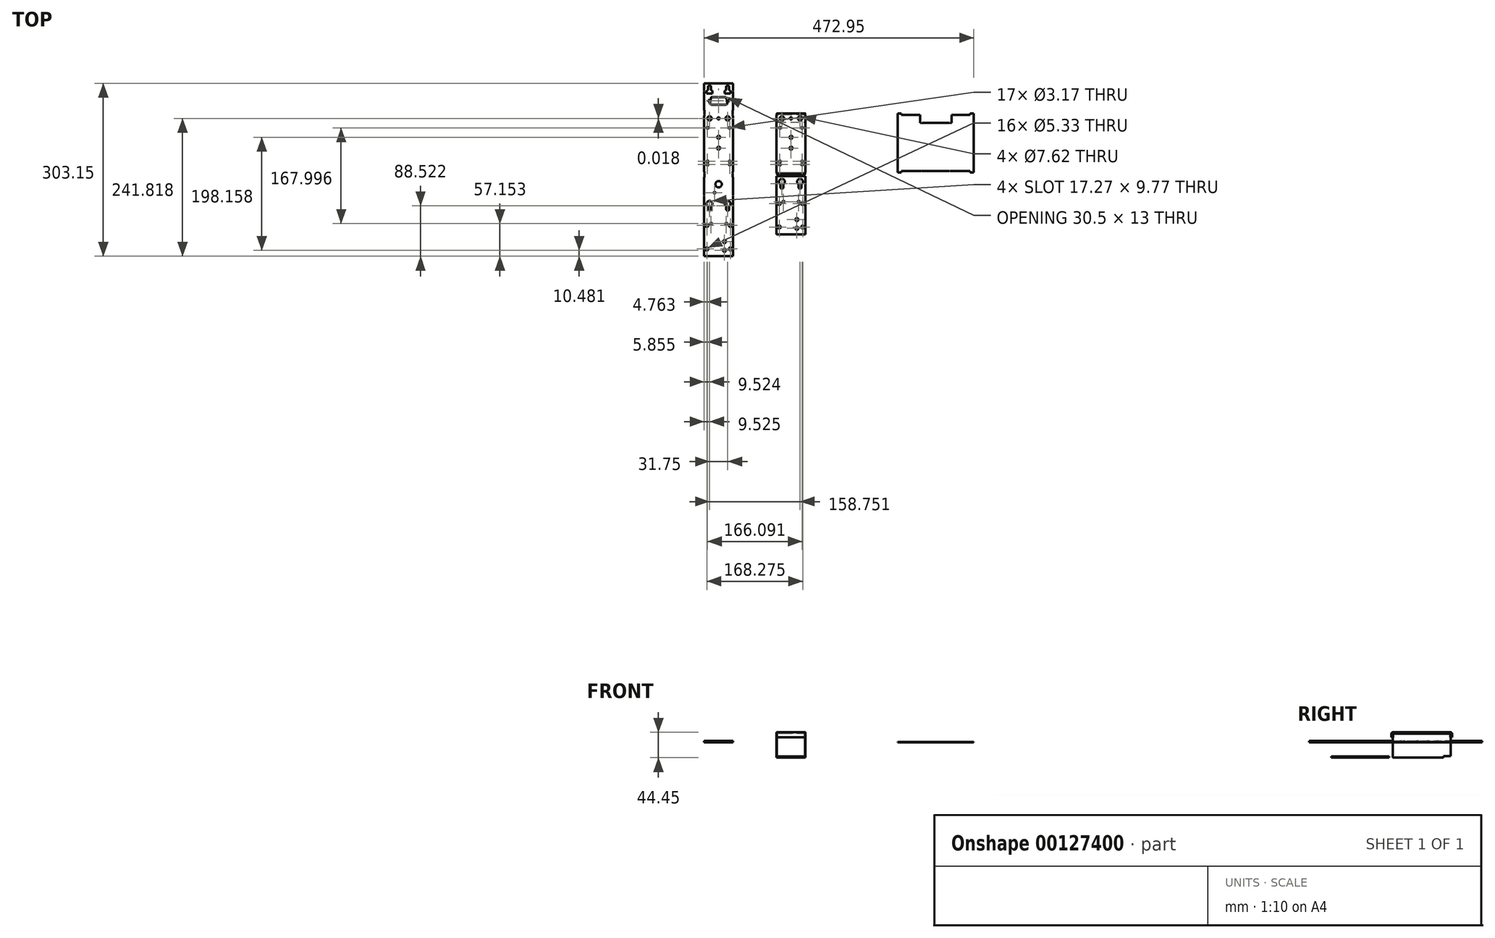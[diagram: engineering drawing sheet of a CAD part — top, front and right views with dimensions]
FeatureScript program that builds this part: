
annotation { "Feature Type Name" : "Feature", "Feature Type Description" : "" }
export const myFeature = defineFeature(function(context is Context, id is Id, definition is map)
    precondition{}
    {
        {
            var Q0;
            Q0=qCreatedBy(makeId("Right.planeOp"),FACE);
            var sketch = newSketch(context, id + "F0", { "sketchPlane" : qUnion([Q0])});
            skLineSegment(sketch, "E0", {"start": v(-154.22, -24.85) * mm, "end": v(-48.63, -24.85) * mm});
            skLineSegment(sketch, "E1", {"start": v(-48.63, -24.85) * mm, "end": v(-48.63, 14.88) * mm});
            skLineSegment(sketch, "E2", {"start": v(-46.27, 17.24) * mm, "end": v(55.33, 17.24) * mm});
            skLineSegment(sketch, "E3", {"start": v(57.7, 14.88) * mm, "end": v(57.7, -24.85) * mm});
            skLineSegment(sketch, "E4", {"start": v(42.63, -24.85) * mm, "end": v(55.33, -24.85) * mm});
            skLineSegment(sketch, "E5.0", {"start": v(42.63, -27.21) * mm, "end": v(55.33, -27.21) * mm});
            skLineSegment(sketch, "E5.1", {"start": v(-154.22, -27.21) * mm, "end": v(-48.63, -27.21) * mm});
            skLineSegment(sketch, "E5.2", {"start": v(-46.27, -24.85) * mm, "end": v(-46.27, 14.88) * mm});
            skLineSegment(sketch, "E5.3", {"start": v(-46.27, 14.88) * mm, "end": v(55.33, 14.88) * mm});
            skLineSegment(sketch, "E5.4", {"start": v(55.33, 14.88) * mm, "end": v(55.33, -24.85) * mm});
            skLineSegment(sketch, "E6", {"start": v(42.63, -24.85) * mm, "end": v(42.63, -27.21) * mm});
            skPoint(sketch, "E7.visualSharp", {"position": v(-48.63, 17.24) * mm});
            skArc(sketch, "E7.filletArc", {"start": v(-46.27, 17.24) * mm, "mid": v(-47.94, 16.55) * mm, "end": v(-48.63, 14.88) * mm});
            skPoint(sketch, "E8.visualSharp", {"position": v(57.7, 17.24) * mm});
            skArc(sketch, "E8.filletArc", {"start": v(57.7, 14.88) * mm, "mid": v(57, 16.55) * mm, "end": v(55.33, 17.24) * mm});
            skPoint(sketch, "E9.visualSharp", {"position": v(55.33, -27.21) * mm});
            skPoint(sketch, "E10.visualSharp", {"position": v(-46.27, -27.21) * mm});
            skArc(sketch, "E10.filletArc", {"start": v(-48.63, -27.21) * mm, "mid": v(-46.96, -26.52) * mm, "end": v(-46.27, -24.85) * mm});
            skPoint(sketch, "E11.newPointA", {"position": v(57.7, -24.85) * mm});
            skArc(sketch, "E11.filletArc", {"start": v(55.33, -27.21) * mm, "mid": v(57, -26.52) * mm, "end": v(57.7, -24.85) * mm});
            skLineSegment(sketch, "E12", {"start": v(-154.22, -24.85) * mm, "end": v(-154.22, -27.21) * mm});
            skSolve(sketch);
        }
        {
            var Q0;
            Q0 = qSketchRegion(id + "F0", true);
            extrude(context, id + "F1", {"entities" : qUnion([Q0]), "endBound" : BoundingType.SYMMETRIC, "depth" : 50.8 * mm});
        }
        {
            var Q0;
            Q0=makeQuery(id+"F1.opExtrude","SWEPT_FACE",FACE,{"disambiguationData":[OSD([sQuery(id+"F0.wireOp",EDGE,"E3")])]});
            var sketch = newSketch(context, id + "F2", { "sketchPlane" : qUnion([Q0])});
            skLineSegment(sketch, "E13.bottom", {"start": v(11.6, -14.66) * mm, "end": v(-11.6, -14.66) * mm});
            skLineSegment(sketch, "E13.top", {"start": v(13.14, -1.66) * mm, "end": v(-13.14, -1.66) * mm});
            skPoint(sketch, "E13.middle", {"position": v(0, -8.16) * mm});
            skLineSegment(sketch, "E14", {"start": v(-15.22, -4.13) * mm, "end": v(-13.67, -12.92) * mm});
            skLineSegment(sketch, "E15", {"start": v(15.22, -4.13) * mm, "end": v(13.67, -12.92) * mm});
            skPoint(sketch, "E16.orphan", {"position": v(-15.66, -14.66) * mm});
            skPoint(sketch, "E13.left.start.orphan", {"position": v(15.66, -14.66) * mm});
            skPoint(sketch, "E17.visualSharp", {"position": v(-15.66, -1.66) * mm});
            skArc(sketch, "E17.filletArc", {"start": v(-13.14, -1.66) * mm, "mid": v(-14.76, -2.41) * mm, "end": v(-15.22, -4.13) * mm});
            skPoint(sketch, "E18.visualSharp", {"position": v(15.66, -1.66) * mm});
            skArc(sketch, "E18.filletArc", {"start": v(15.22, -4.13) * mm, "mid": v(14.76, -2.41) * mm, "end": v(13.14, -1.66) * mm});
            skPoint(sketch, "E19.visualSharp", {"position": v(13.36, -14.66) * mm});
            skArc(sketch, "E19.filletArc", {"start": v(11.6, -14.66) * mm, "mid": v(12.95, -14.17) * mm, "end": v(13.67, -12.92) * mm});
            skPoint(sketch, "E20.visualSharp", {"position": v(-13.36, -14.66) * mm});
            skArc(sketch, "E20.filletArc", {"start": v(-13.67, -12.92) * mm, "mid": v(-12.95, -14.17) * mm, "end": v(-11.6, -14.66) * mm});
            skPoint(sketch, "E21", {"position": v(0, -1.66) * mm});
            skCircle(sketch, "E22", {"center": v(16.69, -8.16) * mm, "radius": 1.5 * mm});
            skCircle(sketch, "E23", {"center": v(-16.69, -8.16) * mm, "radius": 1.5 * mm});
            skSolve(sketch);
        }
        {
            var Q0;
            Q0 = qSketchRegion(id + "F2", true);
            extrude(context, id + "F3", {"entities" : qUnion([Q0]), "operationType" : NewBodyOperationType.REMOVE, "endBound" : BoundingType.UP_TO_NEXT, "oppositeDirection" : true, "depth" : 25.4 * mm});
        }
        {
            var Q0;
            Q0=qCreatedBy(makeId("Top.planeOp"),FACE);
            var sketch = newSketch(context, id + "F4", { "sketchPlane" : qUnion([Q0])});
            skCircle(sketch, "E24", {"center": v(0, 15.78) * mm, "radius": 2.67 * mm});
            skCircle(sketch, "E25", {"center": v(15.88, 48.98) * mm, "radius": 3.81 * mm});
            skCircle(sketch, "E26.1.0.0", {"center": v(-15.88, 48.98) * mm, "radius": 3.81 * mm});
            skLineSegment(sketch, "E26.direction1", {"start": v(15.88, 48.98) * mm, "end": v(-15.88, 48.98) * mm, "construction": true});
            skPoint(sketch, "E27", {"position": v(0, 48.98) * mm});
            skCircle(sketch, "E28", {"center": v(19.55, -32.1) * mm, "radius": 1.59 * mm});
            skCircle(sketch, "E29.MirrorC", {"center": v(19.55, 32.3) * mm, "radius": 1.59 * mm});
            skCircle(sketch, "E30.MirrorC", {"center": v(-19.55, -32.1) * mm, "radius": 1.59 * mm});
            skCircle(sketch, "E31.MirrorC", {"center": v(-19.55, 32.3) * mm, "radius": 1.59 * mm});
            skLineSegment(sketch, "E32", {"start": v(19.55, 32.3) * mm, "end": v(-19.55, 32.3) * mm, "construction": true});
            skPoint(sketch, "E33", {"position": v(0, 32.3) * mm});
            skCircle(sketch, "E34", {"center": v(0, -3.27) * mm, "radius": 2.67 * mm});
            skCircle(sketch, "E35", {"center": v(19.55, -26.49) * mm, "radius": 1.59 * mm});
            skCircle(sketch, "E36", {"center": v(-19.55, -26.49) * mm, "radius": 1.59 * mm});
            skCircle(sketch, "E37", {"center": v(0, 48.98) * mm, "radius": 2.02 * mm});
            skSolve(sketch);
        }
        {
            var Q0;
            Q0=makeQuery(id+"F1.opExtrude","SWEPT_FACE",FACE,{"disambiguationData":[OSD([sQuery(id+"F0.wireOp",EDGE,"E4")])]});
            var sketch = newSketch(context, id + "F5", { "sketchPlane" : qUnion([Q0])});
            skCircle(sketch, "E38", {"center": v(-20.64, -141.52) * mm, "radius": 2.67 * mm});
            skCircle(sketch, "E39.0.1.0", {"center": v(-20.64, -100.25) * mm, "radius": 2.67 * mm});
            skCircle(sketch, "E39.1.0.0", {"center": v(20.64, -141.52) * mm, "radius": 2.67 * mm});
            skCircle(sketch, "E39.1.1.0", {"center": v(20.64, -100.25) * mm, "radius": 2.67 * mm});
            skLineSegment(sketch, "E39.direction1", {"start": v(-20.64, -141.52) * mm, "end": v(20.64, -141.52) * mm, "construction": true});
            skLineSegment(sketch, "E39.direction2", {"start": v(-20.64, -141.52) * mm, "end": v(-20.64, -100.25) * mm, "construction": true});
            skPoint(sketch, "E40", {"position": v(0, -141.52) * mm});
            skLineSegment(sketch, "E41", {"start": v(-15.88, 58.5) * mm, "end": v(-15.88, 48.98) * mm, "construction": true});
            skArc(sketch, "E42", {"start": v(-18.54, 48.98) * mm, "mid": v(-15.88, 46.31) * mm, "end": v(-13.2, 48.98) * mm});
            skArc(sketch, "E43", {"start": v(-13.2, 54.18) * mm, "mid": v(-15.88, 63.58) * mm, "end": v(-18.54, 54.18) * mm});
            skLineSegment(sketch, "E44", {"start": v(-13.2, 48.98) * mm, "end": v(-13.2, 54.18) * mm});
            skLineSegment(sketch, "E45", {"start": v(-18.54, 54.18) * mm, "end": v(-18.54, 48.98) * mm});
            skArc(sketch, "E46.0.1.0", {"start": v(-13.2, -66.47) * mm, "mid": v(-15.88, -57.07) * mm, "end": v(-18.54, -66.47) * mm});
            skLineSegment(sketch, "E46.0.1.1", {"start": v(-18.54, -66.47) * mm, "end": v(-18.54, -71.67) * mm});
            skArc(sketch, "E46.0.1.2", {"start": v(-18.54, -71.67) * mm, "mid": v(-15.88, -74.34) * mm, "end": v(-13.2, -71.67) * mm});
            skLineSegment(sketch, "E46.0.1.3", {"start": v(-13.2, -71.67) * mm, "end": v(-13.2, -66.47) * mm});
            skLineSegment(sketch, "E46.0.1.4", {"start": v(-15.88, -62.15) * mm, "end": v(-15.88, -71.67) * mm, "construction": true});
            skArc(sketch, "E46.1.0.0", {"start": v(18.54, 54.18) * mm, "mid": v(15.88, 63.58) * mm, "end": v(13.2, 54.18) * mm});
            skLineSegment(sketch, "E46.1.0.1", {"start": v(13.2, 54.18) * mm, "end": v(13.2, 48.98) * mm});
            skArc(sketch, "E46.1.0.2", {"start": v(13.2, 48.98) * mm, "mid": v(15.88, 46.31) * mm, "end": v(18.54, 48.98) * mm});
            skLineSegment(sketch, "E46.1.0.3", {"start": v(18.54, 48.98) * mm, "end": v(18.54, 54.18) * mm});
            skLineSegment(sketch, "E46.1.0.4", {"start": v(15.88, 58.5) * mm, "end": v(15.88, 48.98) * mm, "construction": true});
            skArc(sketch, "E46.1.1.0", {"start": v(18.54, -66.47) * mm, "mid": v(15.88, -57.07) * mm, "end": v(13.2, -66.47) * mm});
            skLineSegment(sketch, "E46.1.1.1", {"start": v(13.2, -66.47) * mm, "end": v(13.2, -71.67) * mm});
            skArc(sketch, "E46.1.1.2", {"start": v(13.2, -71.67) * mm, "mid": v(15.88, -74.34) * mm, "end": v(18.54, -71.67) * mm});
            skLineSegment(sketch, "E46.1.1.3", {"start": v(18.54, -71.67) * mm, "end": v(18.54, -66.47) * mm});
            skLineSegment(sketch, "E46.1.1.4", {"start": v(15.88, -62.15) * mm, "end": v(15.88, -71.67) * mm, "construction": true});
            skLineSegment(sketch, "E46.direction1", {"start": v(-15.88, 48.98) * mm, "end": v(15.88, 48.98) * mm, "construction": true});
            skLineSegment(sketch, "E46.direction2", {"start": v(-15.88, 48.98) * mm, "end": v(-15.88, -71.67) * mm, "construction": true});
            skPoint(sketch, "E47", {"position": v(0, 48.98) * mm});
            skLineSegment(sketch, "E48", {"start": v(20.64, -141.52) * mm, "end": v(-20.64, -100.25) * mm, "construction": true});
            skPoint(sketch, "E49", {"position": v(0, -120.88) * mm});
            skCircle(sketch, "E50", {"center": v(10.31, -143.74) * mm, "radius": 2.67 * mm});
            skCircle(sketch, "E51.0.1.0", {"center": v(10.31, -128.5) * mm, "radius": 2.67 * mm});
            skLineSegment(sketch, "E51.direction1", {"start": v(10.31, -143.74) * mm, "end": v(64.72, -143.74) * mm, "construction": true});
            skLineSegment(sketch, "E51.direction2", {"start": v(10.31, -143.74) * mm, "end": v(10.31, -128.5) * mm, "construction": true});
            skPoint(sketch, "E52", {"position": v(10.31, -136.12) * mm});
            skCircle(sketch, "E53", {"center": v(-13.34, -97.07) * mm, "radius": 1.59 * mm});
            skCircle(sketch, "E54.MirrorC", {"center": v(13.34, -97.07) * mm, "radius": 1.59 * mm});
            skPoint(sketch, "E55", {"position": v(0, -136.12) * mm});
            skSolve(sketch);
        }
        {
            var Q0;
            Q0 = qSketchRegion(id + "F4", true);
            var Q1;
            Q1=makeQuery(id+"F1.opExtrude","SWEPT_FACE",FACE,{"disambiguationData":[OSD([sQuery(id+"F0.wireOp",EDGE,"E2")])]});
            extrude(context, id + "F6", {"entities" : qUnion([Q0]), "operationType" : NewBodyOperationType.REMOVE, "endBound" : BoundingType.UP_TO_SURFACE, "endBoundEntityFace" : qUnion([Q1]), "depth" : 76.2 * mm});
        }
        {
            var Q0;
            Q0 = qSketchRegion(id + "F5", true);
            var Q1;
            Q1=makeQuery(id+"F1.opExtrude","SWEPT_FACE",FACE,{"disambiguationData":[OSD([sQuery(id+"F0.wireOp",EDGE,"E5.1")])]});
            extrude(context, id + "F7", {"entities" : qUnion([Q0]), "operationType" : NewBodyOperationType.REMOVE, "endBound" : BoundingType.UP_TO_SURFACE, "oppositeDirection" : true, "endBoundEntityFace" : qUnion([Q1]), "depth" : 25.4 * mm});
        }
        {
            var Q0;
            Q0=makeQuery(id+"F1.opExtrude","SWEPT_FACE",FACE,{"disambiguationData":[OSD([sQuery(id+"F0.wireOp",EDGE,"E3")])]});
            var sketch = newSketch(context, id + "F8", { "sketchPlane" : qUnion([Q0])});
            skLineSegment(sketch, "E56.bottom", {"start": v(-10.8, -33.56) * mm, "end": v(-20.96, -33.56) * mm});
            skLineSegment(sketch, "E56.top", {"start": v(-10.8, -20.86) * mm, "end": v(-20.96, -20.86) * mm});
            skLineSegment(sketch, "E56.left", {"start": v(-10.8, -33.56) * mm, "end": v(-10.8, -20.86) * mm});
            skLineSegment(sketch, "E56.right", {"start": v(-20.96, -33.56) * mm, "end": v(-20.96, -20.86) * mm});
            skLineSegment(sketch, "E57", {"start": v(-15.88, -33.56) * mm, "end": v(-15.88, -20.86) * mm, "construction": true});
            skLineSegment(sketch, "E58.bottom", {"start": v(20.96, -33.56) * mm, "end": v(10.8, -33.56) * mm});
            skLineSegment(sketch, "E58.top", {"start": v(20.95, -20.86) * mm, "end": v(10.8, -20.86) * mm});
            skLineSegment(sketch, "E58.left", {"start": v(20.96, -33.56) * mm, "end": v(20.95, -20.86) * mm});
            skLineSegment(sketch, "E58.right", {"start": v(10.8, -33.56) * mm, "end": v(10.8, -20.86) * mm});
            skLineSegment(sketch, "E59", {"start": v(15.88, -33.56) * mm, "end": v(15.88, -20.86) * mm, "construction": true});
            skSolve(sketch);
        }
        {
            var Q0;
            Q0 = qSketchRegion(id + "F8", true);
            var Q1;
            Q1=makeQuery(id+"F1.opExtrude","SWEPT_FACE",FACE,{"disambiguationData":[OSD([sQuery(id+"F0.wireOp",EDGE,"E5.4")])]});
            extrude(context, id + "F9", {"entities" : qUnion([Q0]), "operationType" : NewBodyOperationType.REMOVE, "endBound" : BoundingType.UP_TO_SURFACE, "oppositeDirection" : true, "endBoundEntityFace" : qUnion([Q1]), "depth" : 25.4 * mm});
        }
        {
            var Q0;
            Q0=qCreatedBy(makeId("Front.planeOp"),FACE);
            var sketch = newSketch(context, id + "F10", { "sketchPlane" : qUnion([Q0])});
            skLineSegment(sketch, "E60.bottom", {"start": v(25.4, 14.88) * mm, "end": v(24.9, 14.88) * mm});
            skLineSegment(sketch, "E60.top", {"start": v(23.88, -26.7) * mm, "end": v(-23.88, -26.7) * mm});
            skLineSegment(sketch, "E60.left", {"start": v(25.4, 14.88) * mm, "end": v(25.4, -25.18) * mm});
            skLineSegment(sketch, "E60.right", {"start": v(-25.4, 14.88) * mm, "end": v(-25.4, -25.18) * mm});
            skLineSegment(sketch, "E61.0", {"start": v(-24.9, 14.88) * mm, "end": v(-24.9, -25.18) * mm});
            skLineSegment(sketch, "E61.1", {"start": v(23.88, -26.2) * mm, "end": v(-23.88, -26.2) * mm});
            skLineSegment(sketch, "E61.2", {"start": v(24.9, 14.88) * mm, "end": v(24.9, -25.18) * mm});
            skLineSegment(sketch, "E62.trimOffspring", {"start": v(-24.9, 14.88) * mm, "end": v(-25.4, 14.88) * mm});
            skPoint(sketch, "E63.visualSharp", {"position": v(25.4, -26.7) * mm});
            skArc(sketch, "E63.filletArc", {"start": v(23.88, -26.7) * mm, "mid": v(24.95, -26.26) * mm, "end": v(25.4, -25.18) * mm});
            skPoint(sketch, "E64.visualSharp", {"position": v(-25.4, -26.7) * mm});
            skArc(sketch, "E64.filletArc", {"start": v(-25.4, -25.18) * mm, "mid": v(-24.95, -26.26) * mm, "end": v(-23.88, -26.7) * mm});
            skPoint(sketch, "E65.visualSharp", {"position": v(24.9, -26.2) * mm});
            skArc(sketch, "E65.filletArc", {"start": v(23.88, -26.2) * mm, "mid": v(24.6, -25.9) * mm, "end": v(24.9, -25.18) * mm});
            skPoint(sketch, "E66.visualSharp", {"position": v(-24.9, -26.2) * mm});
            skArc(sketch, "E66.filletArc", {"start": v(-24.9, -25.18) * mm, "mid": v(-24.6, -25.9) * mm, "end": v(-23.88, -26.2) * mm});
            skSolve(sketch);
        }
        {
            var Q0;
            Q0 = qSketchRegion(id + "F10", true);
            var Q1;
            Q1=makeQuery(id+"F1.opExtrude","SWEPT_FACE",FACE,{"disambiguationData":[OSD([sQuery(id+"F0.wireOp",EDGE,"E1")])]});
            var Q2;
            Q2=makeQuery(id+"F1.opExtrude","SWEPT_FACE",FACE,{"disambiguationData":[OSD([sQuery(id+"F0.wireOp",EDGE,"E3")])]});
            extrude(context, id + "F11", {"entities" : qUnion([Q0]), "endBound" : BoundingType.UP_TO_SURFACE, "endBoundEntityFace" : qUnion([Q1]), "depth" : 25.4 * mm, "hasSecondDirection" : true, "secondDirectionBound" : SecondDirectionBoundingType.UP_TO_SURFACE, "secondDirectionOppositeDirection" : true, "secondDirectionBoundEntityFace" : qUnion([Q2]), "secondDirectionDepth" : 25.4 * mm});
        }
        {
            var Q0;
            Q0=makeQuery(id+"F11.opExtrude","SWEPT_FACE",FACE,{"disambiguationData":[OSD([sQuery(id+"F10.wireOp",EDGE,"E60.right")])]});
            var sketch = newSketch(context, id + "F12", { "sketchPlane" : qUnion([Q0])});
            skLineSegment(sketch, "E67.bottom", {"start": v(52.37, 8.53) * mm, "end": v(46.02, 8.53) * mm});
            skLineSegment(sketch, "E67.top", {"start": v(52.37, -29.57) * mm, "end": v(46.02, -29.57) * mm});
            skLineSegment(sketch, "E67.left", {"start": v(52.37, 8.53) * mm, "end": v(52.37, -29.57) * mm});
            skLineSegment(sketch, "E67.right", {"start": v(46.02, 8.53) * mm, "end": v(46.02, -29.57) * mm});
            skLineSegment(sketch, "E68.bottom", {"start": v(-61.42, -24.6) * mm, "end": v(-42.37, -24.6) * mm});
            skLineSegment(sketch, "E68.top", {"start": v(-61.42, -30.94) * mm, "end": v(-42.37, -30.94) * mm});
            skLineSegment(sketch, "E68.left", {"start": v(-61.42, -24.6) * mm, "end": v(-61.42, -30.94) * mm});
            skLineSegment(sketch, "E68.right", {"start": v(-42.37, -24.6) * mm, "end": v(-42.37, -30.94) * mm});
            skLineSegment(sketch, "E69.bottom", {"start": v(-55.07, 8.53) * mm, "end": v(-61.42, 8.53) * mm});
            skLineSegment(sketch, "E69.top", {"start": v(-55.07, -29.57) * mm, "end": v(-61.42, -29.57) * mm});
            skLineSegment(sketch, "E69.left", {"start": v(-55.07, 8.53) * mm, "end": v(-55.07, -29.57) * mm});
            skLineSegment(sketch, "E69.right", {"start": v(-61.42, 8.53) * mm, "end": v(-61.42, -29.57) * mm});
            skSolve(sketch);
        }
        {
            var Q0;
            Q0 = qSketchRegion(id + "F12", true);
            var Q1;
            Q1=makeQuery(id+"F11.opExtrude","SWEPT_FACE",FACE,{"disambiguationData":[OSD([sQuery(id+"F10.wireOp",EDGE,"E60.left")])]});
            extrude(context, id + "F13", {"entities" : qUnion([Q0]), "operationType" : NewBodyOperationType.REMOVE, "endBound" : BoundingType.UP_TO_SURFACE, "oppositeDirection" : true, "endBoundEntityFace" : qUnion([Q1]), "depth" : 25.4 * mm});
        }
        {
            var Q0;
            Q0=makeQuery(id+"F2.imprint","IMPRINT",FACE,{"disambiguationData":[TD([[makeQuery(id+"F2.imprint","IMPRINT",EDGE,{"derivedFrom":sQuery(id+"F2.wireOp",EDGE,"E13.bottom")}),1.0]])]});
            var sketch = newSketch(context, id + "F14", { "sketchPlane" : qUnion([Q0])});
            skLineSegment(sketch, "E70.bottom", {"start": v(-25.4, 20.97) * mm, "end": v(-24.77, 20.97) * mm});
            skLineSegment(sketch, "E70.top", {"start": v(-25.4, 8.27) * mm, "end": v(-24.76, 8.27) * mm});
            skLineSegment(sketch, "E70.left", {"start": v(-25.4, 20.97) * mm, "end": v(-25.4, 8.27) * mm});
            skLineSegment(sketch, "E70.right", {"start": v(-24.76, 20.97) * mm, "end": v(-24.76, 8.27) * mm});
            skLineSegment(sketch, "E71.bottom", {"start": v(24.77, 20.97) * mm, "end": v(25.4, 20.97) * mm});
            skLineSegment(sketch, "E71.top", {"start": v(24.77, 8.27) * mm, "end": v(25.4, 8.27) * mm});
            skLineSegment(sketch, "E71.left", {"start": v(24.77, 20.97) * mm, "end": v(24.77, 8.27) * mm});
            skLineSegment(sketch, "E71.right", {"start": v(25.4, 20.97) * mm, "end": v(25.4, 8.27) * mm});
            skSolve(sketch);
        }
        {
            var Q0;
            Q0 = qSketchRegion(id + "F14", true);
            extrude(context, id + "F15", {"entities" : qUnion([Q0]), "operationType" : NewBodyOperationType.REMOVE, "oppositeDirection" : true, "depth" : 3.17 * mm});
        }
        {
            var Q0;
            Q0 = qSketchRegion(id + "F14", true);
            var Q1;
            Q1=makeQuery(id+"F1.opExtrude","SWEPT_FACE",FACE,{"disambiguationData":[OSD([sQuery(id+"F0.wireOp",EDGE,"E1")])]});
            extrude(context, id + "F16", {"entities" : qUnion([Q0]), "operationType" : NewBodyOperationType.REMOVE, "endBound" : BoundingType.UP_TO_SURFACE, "oppositeDirection" : true, "endBoundEntityFace" : qUnion([Q1]), "depth" : 25.4 * mm, "hasSecondDirection" : true, "secondDirectionOppositeDirection" : true, "secondDirectionDepth" : 103.12 * mm});
        }
        {
            var Q0;
            Q0=makeQuery(id+"F1.opExtrude","SWEPT_FACE",FACE,{"disambiguationData":[OSD([sQuery(id+"F0.wireOp",EDGE,"E1")])]});
            var sketch = newSketch(context, id + "F17", { "sketchPlane" : qUnion([Q0])});
            skCircle(sketch, "E72", {"center": v(0, -4.17) * mm, "radius": 5.55 * mm});
            skCircle(sketch, "E73", {"center": v(-7.11, -18.9) * mm, "radius": 1.59 * mm});
            skSolve(sketch);
        }
        {
            var Q0;
            Q0 = qSketchRegion(id + "F17", true);
            var Q1;
            Q1=makeQuery(id+"F1.opExtrude","SWEPT_FACE",FACE,{"disambiguationData":[OSD([sQuery(id+"F0.wireOp",EDGE,"E5.2")])]});
            extrude(context, id + "F18", {"entities" : qUnion([Q0]), "operationType" : NewBodyOperationType.REMOVE, "endBound" : BoundingType.UP_TO_SURFACE, "oppositeDirection" : true, "endBoundEntityFace" : qUnion([Q1]), "depth" : 25.4 * mm});
        }
        {
            var Q0;
            Q0=qCreatedBy(makeId("Right.planeOp"),FACE);
            cPlane(context, id + "F19", {"entities" : qUnion([Q0]), "cplaneType" : CPlaneType.OFFSET, "offset" : 127 * mm, "oppositeDirection" : true, "width" : 152.4 * mm, "height" : 152.4 * mm});
        }
        {
            var Q0;
            Q0=qCreatedBy(makeId("Top.planeOp"),FACE);
            var sketch = newSketch(context, id + "F20", { "sketchPlane" : qUnion([Q0])});
            skLineSegment(sketch, "E74.bottom", {"start": v(-101.6, -192.84) * mm, "end": v(-152.4, -192.84) * mm});
            skLineSegment(sketch, "E74.top", {"start": v(-101.6, 110.31) * mm, "end": v(-152.4, 110.31) * mm});
            skLineSegment(sketch, "E74.left", {"start": v(-101.6, -192.84) * mm, "end": v(-101.6, 110.31) * mm});
            skLineSegment(sketch, "E74.right", {"start": v(-152.4, -192.84) * mm, "end": v(-152.4, 110.31) * mm});
            skPoint(sketch, "E74.middle", {"position": v(-127, -41.26) * mm});
            skLineSegment(sketch, "E75", {"start": v(-181.14, 55.35) * mm, "end": v(-85.1, 55.35) * mm, "construction": true});
            skLineSegment(sketch, "E76.0", {"start": v(-181.14, 56.62) * mm, "end": v(-85.1, 56.62) * mm, "construction": true});
            skLineSegment(sketch, "E77", {"start": v(-182.34, 96.34) * mm, "end": v(-85.63, 96.34) * mm, "construction": true});
            skLineSegment(sketch, "E78.0", {"start": v(-182.34, 97.61) * mm, "end": v(-85.63, 97.61) * mm, "construction": true});
            skLineSegment(sketch, "E79", {"start": v(-184.5, -46.25) * mm, "end": v(-79, -46.25) * mm, "construction": true});
            skLineSegment(sketch, "E80.0", {"start": v(-184.5, -47.52) * mm, "end": v(-79, -47.52) * mm, "construction": true});
            skLineSegment(sketch, "E81", {"start": v(-184.42, -85.98) * mm, "end": v(-78.92, -85.98) * mm, "construction": true});
            skLineSegment(sketch, "E82.0", {"start": v(-184.42, -87.25) * mm, "end": v(-78.92, -87.25) * mm, "construction": true});
            skLineSegment(sketch, "E83", {"start": v(-85.63, 97.61) * mm, "end": v(-85.63, 96.34) * mm, "construction": true});
            skPoint(sketch, "E84", {"position": v(-85.63, 96.98) * mm});
            skPoint(sketch, "E85", {"position": v(-99.19, 96.98) * mm});
            skLineSegment(sketch, "E86", {"start": v(-85.1, 56.62) * mm, "end": v(-85.1, 55.35) * mm, "construction": true});
            skPoint(sketch, "E87", {"position": v(-85.1, 55.98) * mm});
            skPoint(sketch, "E88", {"position": v(-99.19, 55.98) * mm});
            skLineSegment(sketch, "E89", {"start": v(-79, -46.25) * mm, "end": v(-79, -47.52) * mm, "construction": true});
            skPoint(sketch, "E90", {"position": v(-79, -46.89) * mm});
            skPoint(sketch, "E91", {"position": v(-99.19, -46.89) * mm});
            skLineSegment(sketch, "E92", {"start": v(-78.92, -85.98) * mm, "end": v(-78.92, -87.25) * mm, "construction": true});
            skPoint(sketch, "E93", {"position": v(-78.92, -86.61) * mm});
            skPoint(sketch, "E94", {"position": v(-99.19, -86.61) * mm});
            skSolve(sketch);
        }
        {
            var Q0;
            Q0 = qSketchRegion(id + "F20", true);
            extrude(context, id + "F21", {"entities" : qUnion([Q0]), "depth" : 2.3 * mm});
        }
        {
            var Q0;
            Q0=qCreatedBy(makeId("Top.planeOp"),FACE);
            var sketch = newSketch(context, id + "F22", { "sketchPlane" : qUnion([Q0])});
            skLineSegment(sketch, "E95", {"start": v(-86.1, 55.35) * mm, "end": v(-62.82, 55.35) * mm, "construction": true});
            skLineSegment(sketch, "E96.0", {"start": v(-86.1, 56.62) * mm, "end": v(-62.82, 56.62) * mm, "construction": true});
            skLineSegment(sketch, "E97", {"start": v(-86.64, 96.34) * mm, "end": v(-64.01, 96.34) * mm, "construction": true});
            skLineSegment(sketch, "E98.0", {"start": v(-86.64, 97.61) * mm, "end": v(-64.01, 97.61) * mm, "construction": true});
            skLineSegment(sketch, "E99", {"start": v(-80, -46.25) * mm, "end": v(-66.16, -46.25) * mm, "construction": true});
            skLineSegment(sketch, "E100.0", {"start": v(-80, -47.52) * mm, "end": v(-66.16, -47.52) * mm, "construction": true});
            skLineSegment(sketch, "E101", {"start": v(-79.93, -85.98) * mm, "end": v(-66.09, -85.98) * mm, "construction": true});
            skLineSegment(sketch, "E102.0", {"start": v(-79.93, -87.25) * mm, "end": v(-66.09, -87.25) * mm, "construction": true});
            skLineSegment(sketch, "E103", {"start": v(-86.64, 97.61) * mm, "end": v(-86.64, 96.34) * mm, "construction": true});
            skPoint(sketch, "E104", {"position": v(-86.64, 96.98) * mm});
            skLineSegment(sketch, "E105", {"start": v(-99.19, 100.15) * mm, "end": v(-102.36, 96.98) * mm});
            skLineSegment(sketch, "E106", {"start": v(-102.36, 96.98) * mm, "end": v(-99.19, 93.8) * mm});
            skLineSegment(sketch, "E107", {"start": v(-99.19, 93.8) * mm, "end": v(-99.19, 100.15) * mm});
            skPoint(sketch, "E108", {"position": v(-99.19, 96.98) * mm});
            skLineSegment(sketch, "E109", {"start": v(-86.1, 56.62) * mm, "end": v(-86.1, 55.35) * mm, "construction": true});
            skPoint(sketch, "E110", {"position": v(-86.1, 55.98) * mm});
            skLineSegment(sketch, "E111", {"start": v(-99.82, 59.16) * mm, "end": v(-103, 55.98) * mm});
            skLineSegment(sketch, "E112", {"start": v(-103, 55.98) * mm, "end": v(-99.82, 52.8) * mm});
            skLineSegment(sketch, "E113", {"start": v(-99.82, 52.8) * mm, "end": v(-99.82, 59.16) * mm});
            skPoint(sketch, "E114", {"position": v(-99.82, 55.98) * mm});
            skLineSegment(sketch, "E115", {"start": v(-80, -46.25) * mm, "end": v(-80, -47.52) * mm, "construction": true});
            skPoint(sketch, "E116", {"position": v(-80, -46.89) * mm});
            skLineSegment(sketch, "E117", {"start": v(-99.82, -43.71) * mm, "end": v(-103, -46.89) * mm});
            skLineSegment(sketch, "E118", {"start": v(-103, -46.89) * mm, "end": v(-99.82, -50.06) * mm});
            skLineSegment(sketch, "E119", {"start": v(-99.82, -50.06) * mm, "end": v(-99.82, -43.71) * mm});
            skPoint(sketch, "E120", {"position": v(-99.82, -46.89) * mm});
            skLineSegment(sketch, "E121", {"start": v(-79.93, -85.98) * mm, "end": v(-79.93, -87.25) * mm, "construction": true});
            skPoint(sketch, "E122", {"position": v(-79.93, -86.61) * mm});
            skLineSegment(sketch, "E123", {"start": v(-99.19, -83.44) * mm, "end": v(-102.36, -86.61) * mm});
            skLineSegment(sketch, "E124", {"start": v(-102.36, -86.61) * mm, "end": v(-99.19, -89.79) * mm});
            skLineSegment(sketch, "E125", {"start": v(-99.19, -89.79) * mm, "end": v(-99.19, -83.44) * mm});
            skPoint(sketch, "E126", {"position": v(-99.19, -86.61) * mm});
            skLineSegment(sketch, "E127.MirrorCS", {"start": v(-151, -46.89) * mm, "end": v(-154.18, -50.06) * mm});
            skLineSegment(sketch, "E128.MirrorCS", {"start": v(-154.18, -43.71) * mm, "end": v(-151, -46.89) * mm});
            skLineSegment(sketch, "E129.MirrorCS", {"start": v(-154.81, 93.8) * mm, "end": v(-154.81, 100.15) * mm});
            skLineSegment(sketch, "E130.MirrorCS", {"start": v(-151.64, 96.98) * mm, "end": v(-154.81, 93.8) * mm});
            skLineSegment(sketch, "E131.MirrorCS", {"start": v(-154.81, 100.15) * mm, "end": v(-151.64, 96.98) * mm});
            skLineSegment(sketch, "E132.MirrorCS", {"start": v(-154.18, 52.8) * mm, "end": v(-154.18, 59.16) * mm});
            skLineSegment(sketch, "E133.MirrorCS", {"start": v(-151, 55.98) * mm, "end": v(-154.18, 52.8) * mm});
            skLineSegment(sketch, "E134.MirrorCS", {"start": v(-154.18, 59.16) * mm, "end": v(-151, 55.98) * mm});
            skLineSegment(sketch, "E135.MirrorCS", {"start": v(-154.81, -89.79) * mm, "end": v(-154.81, -83.44) * mm});
            skLineSegment(sketch, "E136.MirrorCS", {"start": v(-151.64, -86.61) * mm, "end": v(-154.81, -89.79) * mm});
            skLineSegment(sketch, "E137.MirrorCS", {"start": v(-154.81, -83.44) * mm, "end": v(-151.64, -86.61) * mm});
            skLineSegment(sketch, "E138.MirrorCS", {"start": v(-154.18, -50.06) * mm, "end": v(-154.18, -43.71) * mm});
            skPoint(sketch, "E139.MirrorP", {"position": v(-154.81, 96.98) * mm});
            skPoint(sketch, "E140.MirrorP", {"position": v(-154.81, -86.61) * mm});
            skPoint(sketch, "E141.MirrorP", {"position": v(-154.18, -46.89) * mm});
            skPoint(sketch, "E142.MirrorP", {"position": v(-154.18, 55.98) * mm});
            skSolve(sketch);
        }
        {
            var Q0;
            Q0 = qSketchRegion(id + "F22", true);
            var Q1;
            Q1=makeQuery(id+"F21.opExtrude","CAP_FACE",FACE,{"disambiguationData":[OSD([sQuery(id+"F20.wireOp",EDGE,"E74.bottom"),sQuery(id+"F20.wireOp",EDGE,"E74.top"),sQuery(id+"F20.wireOp",EDGE,"E74.left"),sQuery(id+"F20.wireOp",EDGE,"E74.right")])],"isStart":false});
            extrude(context, id + "F23", {"entities" : qUnion([Q0]), "operationType" : NewBodyOperationType.REMOVE, "endBound" : BoundingType.UP_TO_SURFACE, "endBoundEntityFace" : qUnion([Q1]), "depth" : 25.4 * mm});
        }
        {
            var Q0;
            Q0=qCreatedBy(makeId("Top.planeOp"),FACE);
            var sketch = newSketch(context, id + "F24", { "sketchPlane" : qUnion([Q0])});
            skCircle(sketch, "E143", {"center": v(-127, 15.8) * mm, "radius": 2.67 * mm});
            skCircle(sketch, "E144", {"center": v(-111.12, 49) * mm, "radius": 3.81 * mm});
            skCircle(sketch, "E145.1.0.0", {"center": v(-142.88, 49) * mm, "radius": 3.81 * mm});
            skCircle(sketch, "E146", {"center": v(-107.45, -32.08) * mm, "radius": 1.59 * mm});
            skCircle(sketch, "E147.MirrorC", {"center": v(-107.45, 32.3) * mm, "radius": 1.59 * mm});
            skCircle(sketch, "E148.MirrorC", {"center": v(-146.55, -32.08) * mm, "radius": 1.59 * mm});
            skCircle(sketch, "E149.MirrorC", {"center": v(-146.55, 32.3) * mm, "radius": 1.59 * mm});
            skLineSegment(sketch, "E150", {"start": v(-107.45, 32.3) * mm, "end": v(-146.55, 32.3) * mm, "construction": true});
            skPoint(sketch, "E151", {"position": v(-127, 32.3) * mm});
            skCircle(sketch, "E152", {"center": v(-127, -3.25) * mm, "radius": 2.67 * mm});
            skLineSegment(sketch, "E153", {"start": v(-142.88, 49) * mm, "end": v(-111.12, 49) * mm});
            skPoint(sketch, "E154", {"position": v(-127, 49) * mm});
            skCircle(sketch, "E155", {"center": v(-107.45, -26.47) * mm, "radius": 1.59 * mm});
            skCircle(sketch, "E156", {"center": v(-146.55, -26.47) * mm, "radius": 1.59 * mm});
            skCircle(sketch, "E157", {"center": v(-127, 49) * mm, "radius": 1.9 * mm});
            skSolve(sketch);
        }
        {
            var Q0;
            Q0=qCreatedBy(makeId("Top.planeOp"),FACE);
            var sketch = newSketch(context, id + "F25", { "sketchPlane" : qUnion([Q0])});
            skLineSegment(sketch, "E158.bottom", {"start": v(-138.6, 86.16) * mm, "end": v(-115.4, 86.16) * mm});
            skLineSegment(sketch, "E158.top", {"start": v(-140.14, 73.15) * mm, "end": v(-113.86, 73.15) * mm});
            skPoint(sketch, "E158.middle", {"position": v(-127, 79.65) * mm});
            skLineSegment(sketch, "E159", {"start": v(-111.78, 75.63) * mm, "end": v(-113.33, 84.41) * mm});
            skLineSegment(sketch, "E160", {"start": v(-142.22, 75.63) * mm, "end": v(-140.67, 84.41) * mm});
            skPoint(sketch, "E161.orphan", {"position": v(-111.34, 86.16) * mm});
            skPoint(sketch, "E158.left.start.orphan", {"position": v(-142.66, 86.16) * mm});
            skPoint(sketch, "E162.visualSharp", {"position": v(-111.34, 73.15) * mm});
            skArc(sketch, "E162.filletArc", {"start": v(-113.86, 73.15) * mm, "mid": v(-112.24, 73.9) * mm, "end": v(-111.78, 75.63) * mm});
            skPoint(sketch, "E163.visualSharp", {"position": v(-142.66, 73.15) * mm});
            skArc(sketch, "E163.filletArc", {"start": v(-142.22, 75.63) * mm, "mid": v(-141.76, 73.9) * mm, "end": v(-140.14, 73.15) * mm});
            skPoint(sketch, "E164.visualSharp", {"position": v(-140.36, 86.16) * mm});
            skArc(sketch, "E164.filletArc", {"start": v(-138.6, 86.16) * mm, "mid": v(-139.95, 85.66) * mm, "end": v(-140.67, 84.41) * mm});
            skPoint(sketch, "E165.visualSharp", {"position": v(-113.64, 86.16) * mm});
            skArc(sketch, "E165.filletArc", {"start": v(-113.33, 84.41) * mm, "mid": v(-114.05, 85.66) * mm, "end": v(-115.4, 86.16) * mm});
            skPoint(sketch, "E166", {"position": v(-127, 73.15) * mm});
            skCircle(sketch, "E167", {"center": v(-143.69, 79.65) * mm, "radius": 1.5 * mm});
            skCircle(sketch, "E168", {"center": v(-110.31, 79.65) * mm, "radius": 1.5 * mm});
            skSolve(sketch);
        }
        {
            var Q0;
            Q0=qCreatedBy(makeId("Top.planeOp"),FACE);
            var sketch = newSketch(context, id + "F26", { "sketchPlane" : qUnion([Q0])});
            skLineSegment(sketch, "E169", {"start": v(-111.12, 94.44) * mm, "end": v(-111.12, 103.96) * mm, "construction": true});
            skArc(sketch, "E170", {"start": v(-108.46, 103.96) * mm, "mid": v(-111.13, 106.63) * mm, "end": v(-113.8, 103.96) * mm});
            skArc(sketch, "E171", {"start": v(-113.8, 98.76) * mm, "mid": v(-114.5, 98.24) * mm, "end": v(-115.1, 97.61) * mm});
            skLineSegment(sketch, "E172", {"start": v(-113.8, 103.96) * mm, "end": v(-113.8, 98.76) * mm});
            skLineSegment(sketch, "E173", {"start": v(-108.46, 98.76) * mm, "end": v(-108.46, 103.96) * mm});
            skArc(sketch, "E174.1.0.0", {"start": v(-145.54, 98.76) * mm, "mid": v(-146.24, 98.24) * mm, "end": v(-146.84, 97.61) * mm});
            skArc(sketch, "E174.1.0.2", {"start": v(-140.2, 103.96) * mm, "mid": v(-142.87, 106.63) * mm, "end": v(-145.54, 103.96) * mm});
            skLineSegment(sketch, "E174.1.0.3", {"start": v(-145.54, 103.96) * mm, "end": v(-145.54, 98.76) * mm});
            skLineSegment(sketch, "E174.1.0.4", {"start": v(-142.87, 94.44) * mm, "end": v(-142.87, 103.96) * mm, "construction": true});
            skLineSegment(sketch, "E174.direction1", {"start": v(-111.13, 103.96) * mm, "end": v(-142.87, 103.96) * mm, "construction": true});
            skLineSegment(sketch, "E175", {"start": v(-140.2, 103.96) * mm, "end": v(-140.2, 98.76) * mm});
            skPoint(sketch, "E176", {"position": v(-127, 103.96) * mm});
            skLineSegment(sketch, "E177.top", {"start": v(-106.05, 92.35) * mm, "end": v(-116.2, 92.35) * mm});
            skPoint(sketch, "E177.middle", {"position": v(-111.13, 94.35) * mm});
            skArc(sketch, "E178.trimOffspring", {"start": v(-107.16, 97.61) * mm, "mid": v(-107.76, 98.24) * mm, "end": v(-108.46, 98.76) * mm});
            skArc(sketch, "E179.trimOffspring", {"start": v(-138.9, 97.61) * mm, "mid": v(-139.5, 98.24) * mm, "end": v(-140.2, 98.76) * mm});
            skLineSegment(sketch, "E180.bottom", {"start": v(-137.8, 92.35) * mm, "end": v(-147.95, 92.35) * mm});
            skLineSegment(sketch, "E180.top", {"start": v(-137.8, 97.61) * mm, "end": v(-138.9, 97.61) * mm});
            skLineSegment(sketch, "E180.left", {"start": v(-137.8, 92.35) * mm, "end": v(-137.8, 97.61) * mm});
            skLineSegment(sketch, "E180.right", {"start": v(-147.95, 92.35) * mm, "end": v(-147.95, 97.61) * mm});
            skPoint(sketch, "E180.middle", {"position": v(-142.87, 94.98) * mm});
            skLineSegment(sketch, "E181.trimOffspring", {"start": v(-146.84, 97.61) * mm, "end": v(-147.95, 97.61) * mm});
            skLineSegment(sketch, "E182", {"start": v(-116.2, 92.35) * mm, "end": v(-116.2, 97.61) * mm});
            skLineSegment(sketch, "E183", {"start": v(-106.05, 92.35) * mm, "end": v(-106.05, 97.61) * mm});
            skLineSegment(sketch, "E184", {"start": v(-116.2, 97.61) * mm, "end": v(-115.1, 97.61) * mm});
            skLineSegment(sketch, "E185.trimOffspring", {"start": v(-107.16, 97.61) * mm, "end": v(-106.05, 97.61) * mm});
            skPoint(sketch, "E186", {"position": v(-111.13, 92.35) * mm});
            skSolve(sketch);
        }
        {
            var Q0;
            Q0=qCreatedBy(makeId("Top.planeOp"),FACE);
            var sketch = newSketch(context, id + "F27", { "sketchPlane" : qUnion([Q0])});
            skCircle(sketch, "E187", {"center": v(-127, -66.57) * mm, "radius": 5.55 * mm});
            skCircle(sketch, "E188", {"center": v(-134.11, -81.3) * mm, "radius": 1.59 * mm});
            skSolve(sketch);
        }
        {
            var Q0;
            Q0=qCreatedBy(makeId("Top.planeOp"),FACE);
            var sketch = newSketch(context, id + "F28", { "sketchPlane" : qUnion([Q0])});
            skCircle(sketch, "E189", {"center": v(-147.64, -180.14) * mm, "radius": 2.67 * mm});
            skCircle(sketch, "E190.1.0.0", {"center": v(-106.36, -180.14) * mm, "radius": 2.67 * mm});
            skLineSegment(sketch, "E190.direction1", {"start": v(-147.64, -180.14) * mm, "end": v(-106.36, -180.14) * mm, "construction": true});
            skLineSegment(sketch, "E190.direction2", {"start": v(-147.64, -180.14) * mm, "end": v(-147.64, -138.86) * mm, "construction": true});
            skArc(sketch, "E191.0.1.0", {"start": v(-140.2, -105.09) * mm, "mid": v(-142.88, -95.68) * mm, "end": v(-145.54, -105.09) * mm});
            skLineSegment(sketch, "E191.0.1.1", {"start": v(-145.54, -105.09) * mm, "end": v(-145.54, -110.29) * mm});
            skArc(sketch, "E191.0.1.2", {"start": v(-145.54, -110.29) * mm, "mid": v(-142.88, -112.95) * mm, "end": v(-140.2, -110.29) * mm});
            skLineSegment(sketch, "E191.0.1.3", {"start": v(-140.2, -110.29) * mm, "end": v(-140.2, -105.09) * mm});
            skLineSegment(sketch, "E191.0.1.4", {"start": v(-142.88, -100.76) * mm, "end": v(-142.88, -110.29) * mm, "construction": true});
            skArc(sketch, "E191.1.1.0", {"start": v(-108.46, -105.09) * mm, "mid": v(-111.12, -95.68) * mm, "end": v(-113.8, -105.09) * mm});
            skLineSegment(sketch, "E191.1.1.1", {"start": v(-113.8, -105.09) * mm, "end": v(-113.8, -110.29) * mm});
            skArc(sketch, "E191.1.1.2", {"start": v(-113.8, -110.29) * mm, "mid": v(-111.12, -112.95) * mm, "end": v(-108.46, -110.29) * mm});
            skLineSegment(sketch, "E191.1.1.3", {"start": v(-108.46, -110.29) * mm, "end": v(-108.46, -105.09) * mm});
            skLineSegment(sketch, "E191.1.1.4", {"start": v(-111.12, -100.76) * mm, "end": v(-111.12, -110.29) * mm, "construction": true});
            skPoint(sketch, "E192", {"position": v(-127, -159.5) * mm});
            skCircle(sketch, "E193", {"center": v(-116.69, -182.36) * mm, "radius": 2.67 * mm});
            skCircle(sketch, "E194.0.1.0", {"center": v(-116.69, -167.12) * mm, "radius": 2.67 * mm});
            skLineSegment(sketch, "E194.direction2", {"start": v(-116.69, -182.36) * mm, "end": v(-116.69, -167.12) * mm, "construction": true});
            skPoint(sketch, "E195", {"position": v(-116.69, -174.74) * mm});
            skLineSegment(sketch, "E196", {"start": v(-142.88, -100.76) * mm, "end": v(-111.12, -100.76) * mm, "construction": true});
            skPoint(sketch, "E197", {"position": v(-127, -100.76) * mm});
            skCircle(sketch, "E198", {"center": v(-140.34, -135.69) * mm, "radius": 1.59 * mm});
            skCircle(sketch, "E199.MirrorC", {"center": v(-113.66, -135.69) * mm, "radius": 1.59 * mm});
            skPoint(sketch, "E200", {"position": v(-127, -174.74) * mm});
            skCircle(sketch, "E201.0.0.1", {"center": v(-147.64, -138.86) * mm, "radius": 2.67 * mm});
            skCircle(sketch, "E201.0.1.1", {"center": v(-106.36, -138.86) * mm, "radius": 2.67 * mm});
            skLineSegment(sketch, "E202", {"start": v(-106.36, -180.14) * mm, "end": v(-147.64, -138.86) * mm, "construction": true});
            skSolve(sketch);
        }
        {
            var Q0;
            Q0=qCreatedBy(makeId("Top.planeOp"),FACE);
            var sketch = newSketch(context, id + "F29", { "sketchPlane" : qUnion([Q0])});
            skLineSegment(sketch, "E203.bottom", {"start": v(-152.4, -44.35) * mm, "end": v(-151.77, -44.35) * mm});
            skLineSegment(sketch, "E203.top", {"start": v(-152.4, -54.13) * mm, "end": v(-151.77, -54.13) * mm});
            skLineSegment(sketch, "E203.left", {"start": v(-152.4, -44.35) * mm, "end": v(-152.4, -54.13) * mm});
            skLineSegment(sketch, "E203.right", {"start": v(-151.77, -44.35) * mm, "end": v(-151.77, -54.13) * mm});
            skLineSegment(sketch, "E204.MirrorCS", {"start": v(-101.6, -54.13) * mm, "end": v(-102.23, -54.13) * mm});
            skLineSegment(sketch, "E205.MirrorCS", {"start": v(-101.6, -44.35) * mm, "end": v(-102.23, -44.35) * mm});
            skLineSegment(sketch, "E206.MirrorCS", {"start": v(-102.23, -44.35) * mm, "end": v(-102.23, -54.13) * mm});
            skLineSegment(sketch, "E207.MirrorCS", {"start": v(-101.6, -44.35) * mm, "end": v(-101.6, -54.13) * mm});
            skLineSegment(sketch, "E208", {"start": v(-166.16, 4.55) * mm, "end": v(-85.87, 4.55) * mm, "construction": true});
            skLineSegment(sketch, "E209.MirrorCS", {"start": v(-152.4, 63.22) * mm, "end": v(-151.77, 63.22) * mm});
            skLineSegment(sketch, "E210.MirrorCS", {"start": v(-152.4, 53.44) * mm, "end": v(-151.77, 53.44) * mm});
            skLineSegment(sketch, "E211.MirrorCS", {"start": v(-101.6, 53.44) * mm, "end": v(-102.23, 53.44) * mm});
            skLineSegment(sketch, "E212.MirrorCS", {"start": v(-101.6, 63.22) * mm, "end": v(-102.23, 63.22) * mm});
            skLineSegment(sketch, "E213.MirrorCS", {"start": v(-151.77, 53.44) * mm, "end": v(-151.77, 63.22) * mm});
            skLineSegment(sketch, "E214.MirrorCS", {"start": v(-152.4, 53.44) * mm, "end": v(-152.4, 63.22) * mm});
            skLineSegment(sketch, "E215.MirrorCS", {"start": v(-102.23, 53.44) * mm, "end": v(-102.23, 63.22) * mm});
            skLineSegment(sketch, "E216.MirrorCS", {"start": v(-101.6, 53.44) * mm, "end": v(-101.6, 63.22) * mm});
            skSolve(sketch);
        }
        {
            var Q0;
            Q0 = qSketchRegion(id + "F24", true);
            var Q1;
            Q1 = qSketchRegion(id + "F25", true);
            var Q2;
            Q2 = qSketchRegion(id + "F26", true);
            var Q3;
            Q3 = qSketchRegion(id + "F27", true);
            var Q4;
            Q4 = qSketchRegion(id + "F28", true);
            var Q5;
            Q5 = qSketchRegion(id + "F29", true);
            extrude(context, id + "F30", {"entities" : qUnion([Q0, Q1, Q2, Q3, Q4, Q5]), "operationType" : NewBodyOperationType.REMOVE, "endBound" : BoundingType.THROUGH_ALL, "depth" : 25.4 * mm});
        }
        {
            var Q0;
            Q0=qCreatedBy(makeId("Top.planeOp"),FACE);
            var sketch = newSketch(context, id + "F31", { "sketchPlane" : qUnion([Q0])});
            skLineSegment(sketch, "E217.bottom", {"start": v(187.45, 57.7) * mm, "end": v(193.8, 57.7) * mm});
            skLineSegment(sketch, "E217.top", {"start": v(187.45, -45.81) * mm, "end": v(193.8, -45.81) * mm});
            skLineSegment(sketch, "E217.left", {"start": v(187.45, 57.7) * mm, "end": v(187.45, -45.81) * mm});
            skLineSegment(sketch, "E217.right", {"start": v(320.55, 57.7) * mm, "end": v(320.55, -45.81) * mm});
            skLineSegment(sketch, "E218", {"start": v(254, 49.77) * mm, "end": v(254, -146.13) * mm, "construction": true});
            skPoint(sketch, "E219", {"position": v(254, 57.7) * mm});
            skPoint(sketch, "E220", {"position": v(254, -45.81) * mm});
            skLineSegment(sketch, "E221.bottom", {"start": v(193.8, -43.2) * mm, "end": v(228.6, -43.2) * mm});
            skLineSegment(sketch, "E221.left", {"start": v(193.8, -43.2) * mm, "end": v(193.8, -45.81) * mm});
            skLineSegment(sketch, "E221.right", {"start": v(314.2, -43.2) * mm, "end": v(314.2, -45.81) * mm});
            skPoint(sketch, "E221.middle", {"position": v(254, -55.9) * mm});
            skPoint(sketch, "E221.top.end.orphan", {"position": v(314.2, -68.6) * mm});
            skPoint(sketch, "E221.top.start.orphan", {"position": v(193.8, -68.6) * mm});
            skLineSegment(sketch, "E222.trimOffspring", {"start": v(314.2, -45.81) * mm, "end": v(320.55, -45.81) * mm});
            skLineSegment(sketch, "E223", {"start": v(193.8, 57.7) * mm, "end": v(193.8, 55.07) * mm});
            skLineSegment(sketch, "E224", {"start": v(193.8, 55.07) * mm, "end": v(226.31, 55.07) * mm});
            skLineSegment(sketch, "E225", {"start": v(314.2, 55.07) * mm, "end": v(314.2, 57.7) * mm});
            skLineSegment(sketch, "E226.trimOffspring", {"start": v(314.2, 57.7) * mm, "end": v(320.55, 57.7) * mm});
            skLineSegment(sketch, "E227", {"start": v(226.31, 55.07) * mm, "end": v(226.31, 40.85) * mm});
            skLineSegment(sketch, "E228", {"start": v(226.31, 40.85) * mm, "end": v(228.6, 40.85) * mm});
            skLineSegment(sketch, "E229", {"start": v(281.69, 40.85) * mm, "end": v(281.69, 55.07) * mm});
            skLineSegment(sketch, "E230.trimOffspring", {"start": v(281.69, 55.07) * mm, "end": v(314.2, 55.07) * mm});
            skLineSegment(sketch, "E231", {"start": v(277.88, -43.2) * mm, "end": v(278.64, -42.44) * mm});
            skLineSegment(sketch, "E232", {"start": v(278.64, -42.44) * mm, "end": v(279.4, -43.2) * mm});
            skLineSegment(sketch, "E233.trimOffspring", {"start": v(279.4, -43.2) * mm, "end": v(314.2, -43.2) * mm});
            skLineSegment(sketch, "E234.MirrorCS", {"start": v(230.12, -43.2) * mm, "end": v(229.36, -42.44) * mm});
            skLineSegment(sketch, "E235.MirrorCS", {"start": v(229.36, -42.44) * mm, "end": v(228.6, -43.2) * mm});
            skLineSegment(sketch, "E236.trimOffspring", {"start": v(230.12, -43.2) * mm, "end": v(277.88, -43.2) * mm});
            skLineSegment(sketch, "E237", {"start": v(278.64, 40.09) * mm, "end": v(277.88, 40.85) * mm});
            skLineSegment(sketch, "E238", {"start": v(278.64, 40.09) * mm, "end": v(279.4, 40.85) * mm});
            skLineSegment(sketch, "E239.trimOffspring", {"start": v(279.4, 40.85) * mm, "end": v(281.69, 40.85) * mm});
            skLineSegment(sketch, "E240.MirrorCS", {"start": v(229.36, 40.09) * mm, "end": v(228.6, 40.85) * mm});
            skLineSegment(sketch, "E241.MirrorCS", {"start": v(229.36, 40.09) * mm, "end": v(230.12, 40.85) * mm});
            skLineSegment(sketch, "E242.trimOffspring", {"start": v(230.12, 40.85) * mm, "end": v(277.88, 40.85) * mm});
            skSolve(sketch);
        }
        {
            var Q0;
            Q0 = qSketchRegion(id + "F31", true);
            extrude(context, id + "F32", {"entities" : qUnion([Q0]), "endBound" : BoundingType.SYMMETRIC, "depth" : 0.46 * mm});
        }
    });
